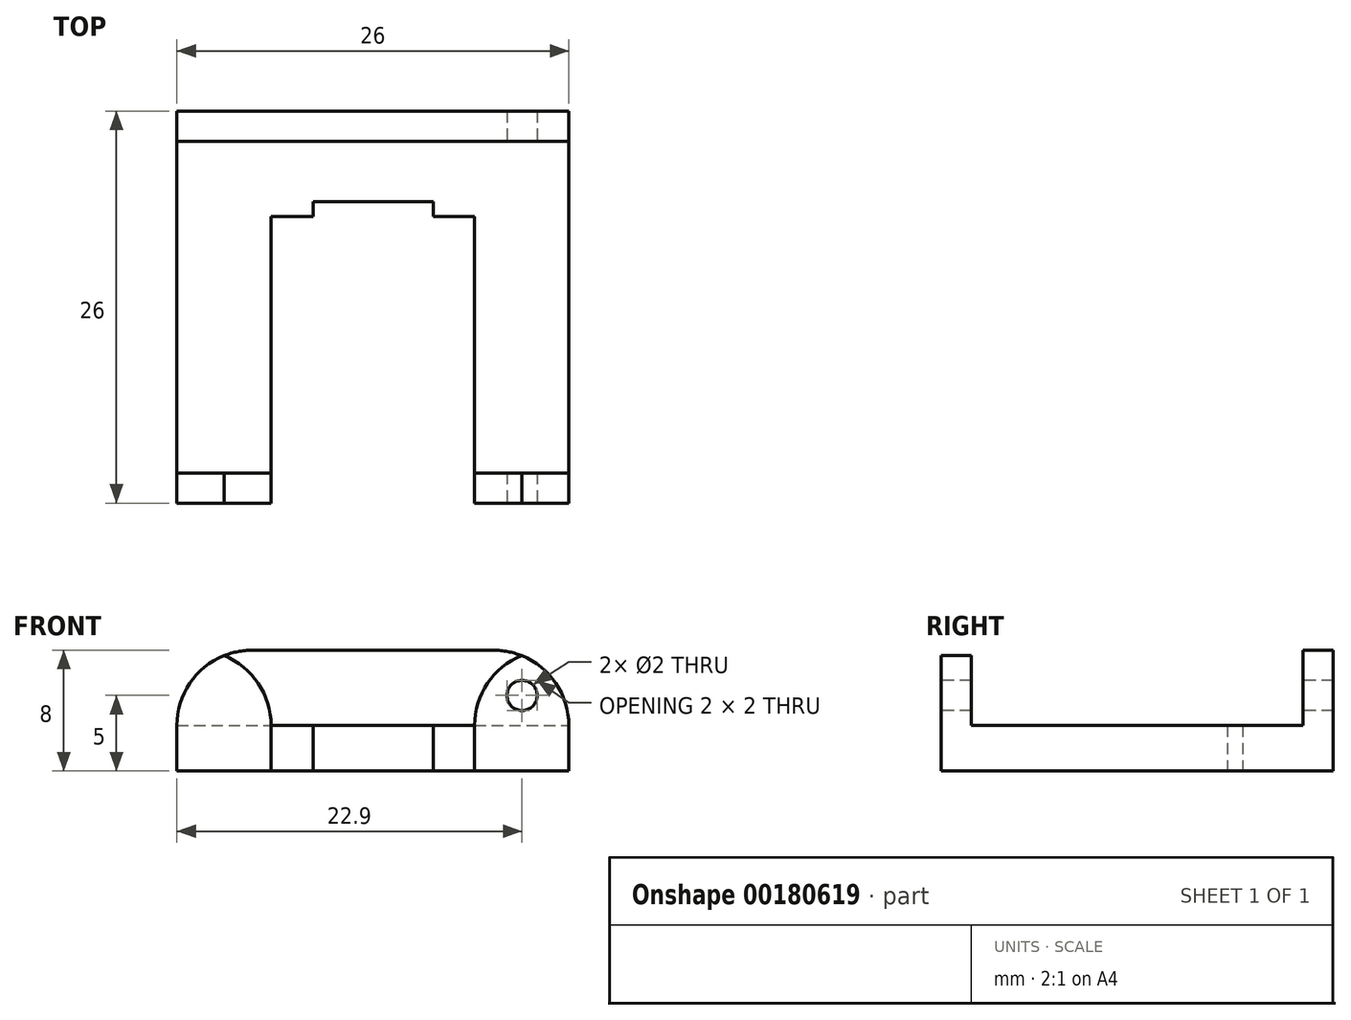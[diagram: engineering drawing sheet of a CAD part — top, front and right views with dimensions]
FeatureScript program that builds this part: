
annotation { "Feature Type Name" : "Feature", "Feature Type Description" : "" }
export const myFeature = defineFeature(function(context is Context, id is Id, definition is map)
    precondition{}
    {
        {
            var Q0;
            Q0=qCreatedBy(makeId("Top.planeOp"),FACE);
            var sketch = newSketch(context, id + "F0", { "sketchPlane" : qUnion([Q0])});
            skLineSegment(sketch, "E0.bottom", {"start": v(13, -13) * mm, "end": v(-13, -13) * mm});
            skLineSegment(sketch, "E0.top", {"start": v(13, 13) * mm, "end": v(-13, 13) * mm});
            skLineSegment(sketch, "E0.left", {"start": v(13, -13) * mm, "end": v(13, 13) * mm});
            skLineSegment(sketch, "E0.right", {"start": v(-13, -13) * mm, "end": v(-13, 13) * mm});
            skPoint(sketch, "E0.middle", {"position": v(0, 0) * mm});
            skLineSegment(sketch, "E1.bottom", {"start": v(6.75, -13) * mm, "end": v(-6.75, -13) * mm});
            skLineSegment(sketch, "E1.top", {"start": v(6.75, 6) * mm, "end": v(-6.75, 6) * mm});
            skLineSegment(sketch, "E1.left", {"start": v(6.75, -13) * mm, "end": v(6.75, 6) * mm});
            skLineSegment(sketch, "E1.right", {"start": v(-6.75, -13) * mm, "end": v(-6.75, 6) * mm});
            skPoint(sketch, "E1.middle", {"position": v(0, -3.5) * mm});
            skLineSegment(sketch, "E2", {"start": v(-13, 11) * mm, "end": v(13, 11) * mm});
            skLineSegment(sketch, "E3", {"start": v(-13, -11) * mm, "end": v(-6.75, -11) * mm});
            skLineSegment(sketch, "E4", {"start": v(6.75, -11) * mm, "end": v(13, -11) * mm});
            skLineSegment(sketch, "E5", {"start": v(-3.97, 6) * mm, "end": v(-3.97, 7) * mm});
            skLineSegment(sketch, "E6", {"start": v(-3.97, 7) * mm, "end": v(4.03, 7) * mm});
            skLineSegment(sketch, "E7", {"start": v(4.03, 7) * mm, "end": v(4.03, 6) * mm});
            skSolve(sketch);
        }
        {
            var Q0;
            Q0=makeQuery(id+"F0.imprint","IMPRINT",FACE,{"disambiguationData":[TD([[makeQuery(id+"F0.imprint","IMPRINT",EDGE,{"derivedFrom":sQuery(id+"F0.wireOp",EDGE,"E0.top")}),1.0]])]});
            var Q1;
            {var subQ5=sQuery(id+"F0.wireOp",EDGE,"E3");Q1=makeQuery(id+"F0.imprint","IMPRINT",FACE,{"disambiguationData":[TD([[makeQuery(id+"F0.imprint","IMPRINT",EDGE,{"derivedFrom":subQ5}),-1.0]])]});}
            var Q2;
            {var subQ5=sQuery(id+"F0.wireOp",EDGE,"E4");Q2=makeQuery(id+"F0.imprint","IMPRINT",FACE,{"disambiguationData":[TD([[makeQuery(id+"F0.imprint","IMPRINT",EDGE,{"derivedFrom":subQ5}),-1.0]])]});}
            extrude(context, id + "F1", {"entities" : qUnion([Q0, Q1, Q2]), "depth" : 8 * mm});
        }
        {
            var Q0;
            {var subQ1=sQuery(id+"F0.wireOp",EDGE,"E1.top");Q0=makeQuery(id+"F0.imprint","IMPRINT",FACE,{"disambiguationData":[TD([[makeQuery(id+"F0.imprint","IMPRINT",EDGE,{"derivedFrom":subQ1}),-1.0]])]});}
            extrude(context, id + "F2", {"entities" : qUnion([Q0]), "operationType" : NewBodyOperationType.ADD, "depth" : 3 * mm});
        }
        {
            var Q0;
            {var subQ0=sQuery(id+"F0.wireOp",EDGE,"E0.right");Q0=makeQuery(id+"F1.opExtrude","CAP_EDGE",EDGE,{"disambiguationData":[OSD([subQ0]),TDD([makeQuery(id+"F0.imprint","IMPRINT",EDGE,{"disambiguationData":[TD([[makeQuery(id+"F0.imprint","INTERSECT",VERTEX,{"derivedFrom":[sQuery(id+"F0.wireOp",EDGE,"E0.bottom"),subQ0]}),-1.0]])],"derivedFrom":subQ0})])],"isStart":false});}
            var Q1;
            Q1=makeQuery(id+"F1.opExtrude","CAP_EDGE",EDGE,{"disambiguationData":[OSD([sQuery(id+"F0.wireOp",EDGE,"E1.right")])],"isStart":false});
            var Q2;
            Q2=makeQuery(id+"F1.opExtrude","CAP_EDGE",EDGE,{"disambiguationData":[OSD([sQuery(id+"F0.wireOp",EDGE,"E1.left")])],"isStart":false});
            var Q3;
            {var subQ0=sQuery(id+"F0.wireOp",EDGE,"E0.left");Q3=makeQuery(id+"F1.opExtrude","CAP_EDGE",EDGE,{"disambiguationData":[OSD([subQ0]),TDD([makeQuery(id+"F0.imprint","IMPRINT",EDGE,{"disambiguationData":[TD([[makeQuery(id+"F0.imprint","INTERSECT",VERTEX,{"derivedFrom":[sQuery(id+"F0.wireOp",EDGE,"E0.bottom"),subQ0]}),-1.0]])],"derivedFrom":subQ0})])],"isStart":false});}
            var Q4;
            {var subQ0=sQuery(id+"F0.wireOp",EDGE,"E0.left");Q4=makeQuery(id+"F1.opExtrude","CAP_EDGE",EDGE,{"disambiguationData":[OSD([subQ0]),TDD([makeQuery(id+"F0.imprint","IMPRINT",EDGE,{"disambiguationData":[TD([[makeQuery(id+"F0.imprint","INTERSECT",VERTEX,{"derivedFrom":[sQuery(id+"F0.wireOp",EDGE,"E0.top"),subQ0]}),1.0]])],"derivedFrom":subQ0})])],"isStart":false});}
            var Q5;
            {var subQ0=sQuery(id+"F0.wireOp",EDGE,"E0.right");Q5=makeQuery(id+"F1.opExtrude","CAP_EDGE",EDGE,{"disambiguationData":[OSD([subQ0]),TDD([makeQuery(id+"F0.imprint","IMPRINT",EDGE,{"disambiguationData":[TD([[makeQuery(id+"F0.imprint","INTERSECT",VERTEX,{"derivedFrom":[sQuery(id+"F0.wireOp",EDGE,"E0.top"),subQ0]}),1.0]])],"derivedFrom":subQ0})])],"isStart":false});}
            fillet(context, id + "F3", {"entities" : qUnion([Q0, Q1, Q2, Q3, Q4, Q5]), "radius" : 5 * mm, "tangentPropagation" : true, "allowEdgeOverflow" : false});
        }
        {
            var Q0;
            {var subQ0=sQuery(id+"F0.wireOp",EDGE,"E0.bottom");Q0=makeQuery(id+"F1.opExtrude","SWEPT_FACE",FACE,{"disambiguationData":[OSD([subQ0]),TDD([makeQuery(id+"F0.imprint","IMPRINT",EDGE,{"disambiguationData":[TD([[makeQuery(id+"F0.imprint","INTERSECT",VERTEX,{"derivedFrom":[subQ0,sQuery(id+"F0.wireOp",EDGE,"E0.left")]}),-1.0]])],"derivedFrom":subQ0})])]});}
            var sketch = newSketch(context, id + "F4", { "sketchPlane" : qUnion([Q0])});
            skCircle(sketch, "E8", {"center": v(9.9, 5) * mm, "radius": 1 * mm});
            skCircle(sketch, "E9.MirrorC", {"center": v(-9.9, 5) * mm, "radius": 1 * mm});
            skSolve(sketch);
        }
        {
            var Q0;
            Q0=makeQuery(id+"F4.imprint","IMPRINT",FACE,{"disambiguationData":[TD([[makeQuery(id+"F4.imprint","IMPRINT",EDGE,{"derivedFrom":sQuery(id+"F4.wireOp",EDGE,"E9.MirrorC")}),-1.0]])]});
            var Q1;
            Q1=makeQuery(id+"F4.imprint","IMPRINT",FACE,{"disambiguationData":[TD([[makeQuery(id+"F4.imprint","IMPRINT",EDGE,{"derivedFrom":sQuery(id+"F4.wireOp",EDGE,"E8")}),1.0]])]});
            extrude(context, id + "F5", {"entities" : qUnion([Q0, Q1]), "operationType" : NewBodyOperationType.REMOVE, "oppositeDirection" : true, "depth" : 30 * mm});
        }
    });
